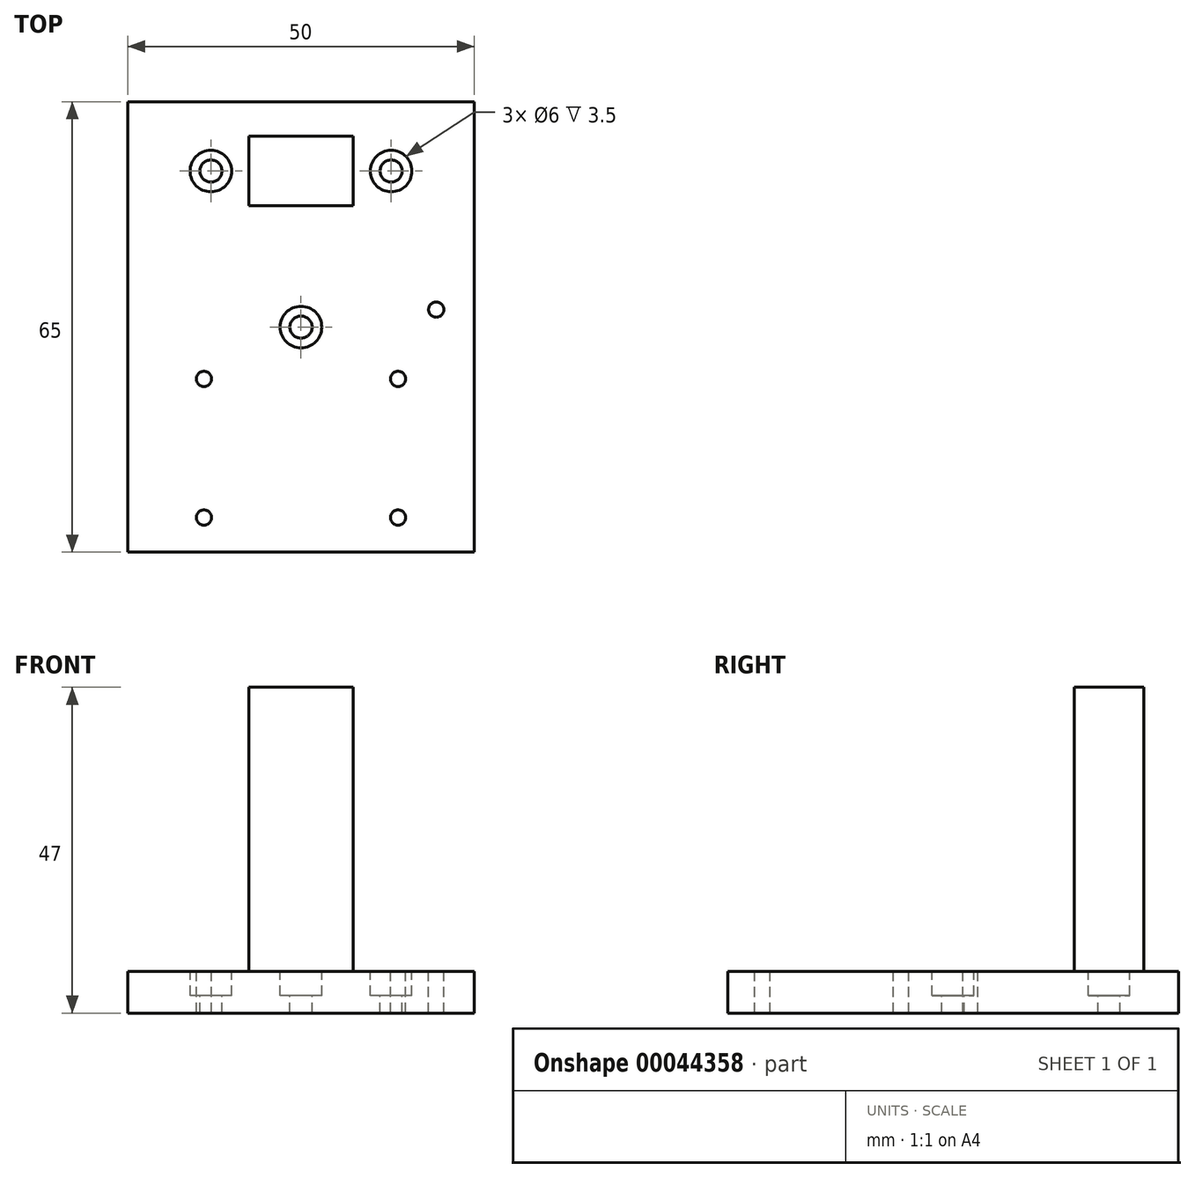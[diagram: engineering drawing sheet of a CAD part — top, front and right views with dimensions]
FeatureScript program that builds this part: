
annotation { "Feature Type Name" : "Feature", "Feature Type Description" : "" }
export const myFeature = defineFeature(function(context is Context, id is Id, definition is map)
    precondition{}
    {
        {
            var Q0;
            Q0=qCreatedBy(makeId("Top.planeOp"),FACE);
            var sketch = newSketch(context, id + "F0", { "sketchPlane" : qUnion([Q0])});
            skLineSegment(sketch, "E0.bottom", {"start": v(0, 0) * mm, "end": v(50, 0) * mm});
            skLineSegment(sketch, "E0.top", {"start": v(0, 65) * mm, "end": v(50, 65) * mm});
            skLineSegment(sketch, "E0.left", {"start": v(0, 0) * mm, "end": v(0, 65) * mm});
            skLineSegment(sketch, "E0.right", {"start": v(50, 0) * mm, "end": v(50, 65) * mm});
            skSolve(sketch);
        }
        {
            var Q0;
            Q0 = qSketchRegion(id + "F0", true);
            extrude(context, id + "F1", {"entities" : qUnion([Q0]), "depth" : 6 * mm});
        }
        {
            var Q0;
            Q0=makeQuery(id+"F1.opExtrude","CAP_FACE",FACE,{"disambiguationData":[OSD([sQuery(id+"F0.wireOp",EDGE,"E0.bottom"),sQuery(id+"F0.wireOp",EDGE,"E0.top"),sQuery(id+"F0.wireOp",EDGE,"E0.left"),sQuery(id+"F0.wireOp",EDGE,"E0.right")])],"isStart":false});
            var sketch = newSketch(context, id + "F2", { "sketchPlane" : qUnion([Q0])});
            skLineSegment(sketch, "E1.bottom", {"start": v(17.5, 60) * mm, "end": v(32.5, 60) * mm});
            skLineSegment(sketch, "E1.top", {"start": v(17.5, 50) * mm, "end": v(32.5, 50) * mm});
            skLineSegment(sketch, "E1.left", {"start": v(17.5, 60) * mm, "end": v(17.5, 50) * mm});
            skLineSegment(sketch, "E1.right", {"start": v(32.5, 60) * mm, "end": v(32.5, 50) * mm});
            skLineSegment(sketch, "E2", {"start": v(32.5, 60) * mm, "end": v(50, 60) * mm});
            skLineSegment(sketch, "E3", {"start": v(17.5, 60) * mm, "end": v(0, 60) * mm});
            skSolve(sketch);
        }
        {
            var Q0;
            Q0 = qSketchRegion(id + "F2", true);
            extrude(context, id + "F3", {"entities" : qUnion([Q0]), "operationType" : NewBodyOperationType.ADD, "depth" : 41 * mm});
        }
        {
            var Q0;
            Q0=makeQuery(id+"F1.opExtrude","CAP_FACE",FACE,{"disambiguationData":[OSD([sQuery(id+"F0.wireOp",EDGE,"E0.bottom"),sQuery(id+"F0.wireOp",EDGE,"E0.top"),sQuery(id+"F0.wireOp",EDGE,"E0.left"),sQuery(id+"F0.wireOp",EDGE,"E0.right")])],"isStart":false});
            var sketch = newSketch(context, id + "F4", { "sketchPlane" : qUnion([Q0])});
            skPoint(sketch, "E4", {"position": v(12, 55) * mm});
            skPoint(sketch, "E5", {"position": v(38, 55) * mm});
            skLineSegment(sketch, "E6", {"start": v(12, 55) * mm, "end": v(38, 55) * mm});
            skLineSegment(sketch, "E7", {"start": v(38, 55) * mm, "end": v(50, 55) * mm});
            skLineSegment(sketch, "E8", {"start": v(12, 55) * mm, "end": v(0, 55) * mm});
            skPoint(sketch, "E9", {"position": v(25, 32.48) * mm});
            skSolve(sketch);
        }
        {
            var Q0;
            Q0=sQuery(id+"F4.wireOp",VERTEX,"E4");
            var Q1;
            Q1=sQuery(id+"F4.wireOp",VERTEX,"E5");
            var Q2;
            Q2=sQuery(id+"F4.wireOp",VERTEX,"E9");
            var Q3;
            Q3=makeQuery(id+"F1.opExtrude","SWEPT_BODY",BODY,{"disambiguationData":[OSD([sQuery(id+"F0.wireOp",EDGE,"E0.bottom"),sQuery(id+"F0.wireOp",EDGE,"E0.top"),sQuery(id+"F0.wireOp",EDGE,"E0.left"),sQuery(id+"F0.wireOp",EDGE,"E0.right")])]});
            hole(context, id + "F5", {"style" : HoleStyle.C_BORE, "holeDiameter" : 3.2 * mm, "cBoreDiameter" : 6 * mm, "cBoreDepth" : 3.5 * mm, "endStyle" : HoleEndStyle.THROUGH, "locations" : qUnion([Q0, Q1, Q2]), "scope" : qUnion([Q3])});
        }
        {
            var Q0;
            Q0=makeQuery(id+"F1.opExtrude","CAP_FACE",FACE,{"disambiguationData":[OSD([sQuery(id+"F0.wireOp",EDGE,"E0.bottom"),sQuery(id+"F0.wireOp",EDGE,"E0.top"),sQuery(id+"F0.wireOp",EDGE,"E0.left"),sQuery(id+"F0.wireOp",EDGE,"E0.right")])],"isStart":false});
            var sketch = newSketch(context, id + "F6", { "sketchPlane" : qUnion([Q0])});
            skLineSegment(sketch, "E10.bottom", {"start": v(11, 25) * mm, "end": v(39, 25) * mm});
            skLineSegment(sketch, "E10.top", {"start": v(11, 5) * mm, "end": v(39, 5) * mm});
            skLineSegment(sketch, "E10.left", {"start": v(11, 25) * mm, "end": v(11, 5) * mm});
            skLineSegment(sketch, "E10.right", {"start": v(39, 25) * mm, "end": v(39, 5) * mm});
            skLineSegment(sketch, "E11", {"start": v(39, 25) * mm, "end": v(50, 25) * mm});
            skLineSegment(sketch, "E12", {"start": v(11, 25) * mm, "end": v(0, 25) * mm});
            skPoint(sketch, "E13", {"position": v(44.5, 35) * mm});
            skPoint(sketch, "E13.positionSnap0", {"position": v(44.5, 25) * mm});
            skSolve(sketch);
        }
        {
            var Q0;
            Q0=sQuery(id+"F6.wireOp",VERTEX,"E12.start");
            var Q1;
            Q1=sQuery(id+"F6.wireOp",VERTEX,"E11.start");
            var Q2;
            Q2=sQuery(id+"F6.wireOp",VERTEX,"E10.right.end");
            var Q3;
            Q3=sQuery(id+"F6.wireOp",VERTEX,"E10.top.start");
            var Q4;
            Q4=sQuery(id+"F6.wireOp",VERTEX,"E13");
            var Q5;
            Q5=makeQuery(id+"F1.opExtrude","SWEPT_BODY",BODY,{"disambiguationData":[OSD([sQuery(id+"F0.wireOp",EDGE,"E0.bottom"),sQuery(id+"F0.wireOp",EDGE,"E0.top"),sQuery(id+"F0.wireOp",EDGE,"E0.left"),sQuery(id+"F0.wireOp",EDGE,"E0.right")])]});
            hole(context, id + "F7", {"style" : HoleStyle.SIMPLE, "holeDiameter" : 2.2 * mm, "endStyle" : HoleEndStyle.THROUGH, "locations" : qUnion([Q0, Q1, Q2, Q3, Q4]), "scope" : qUnion([Q5])});
        }
    });
